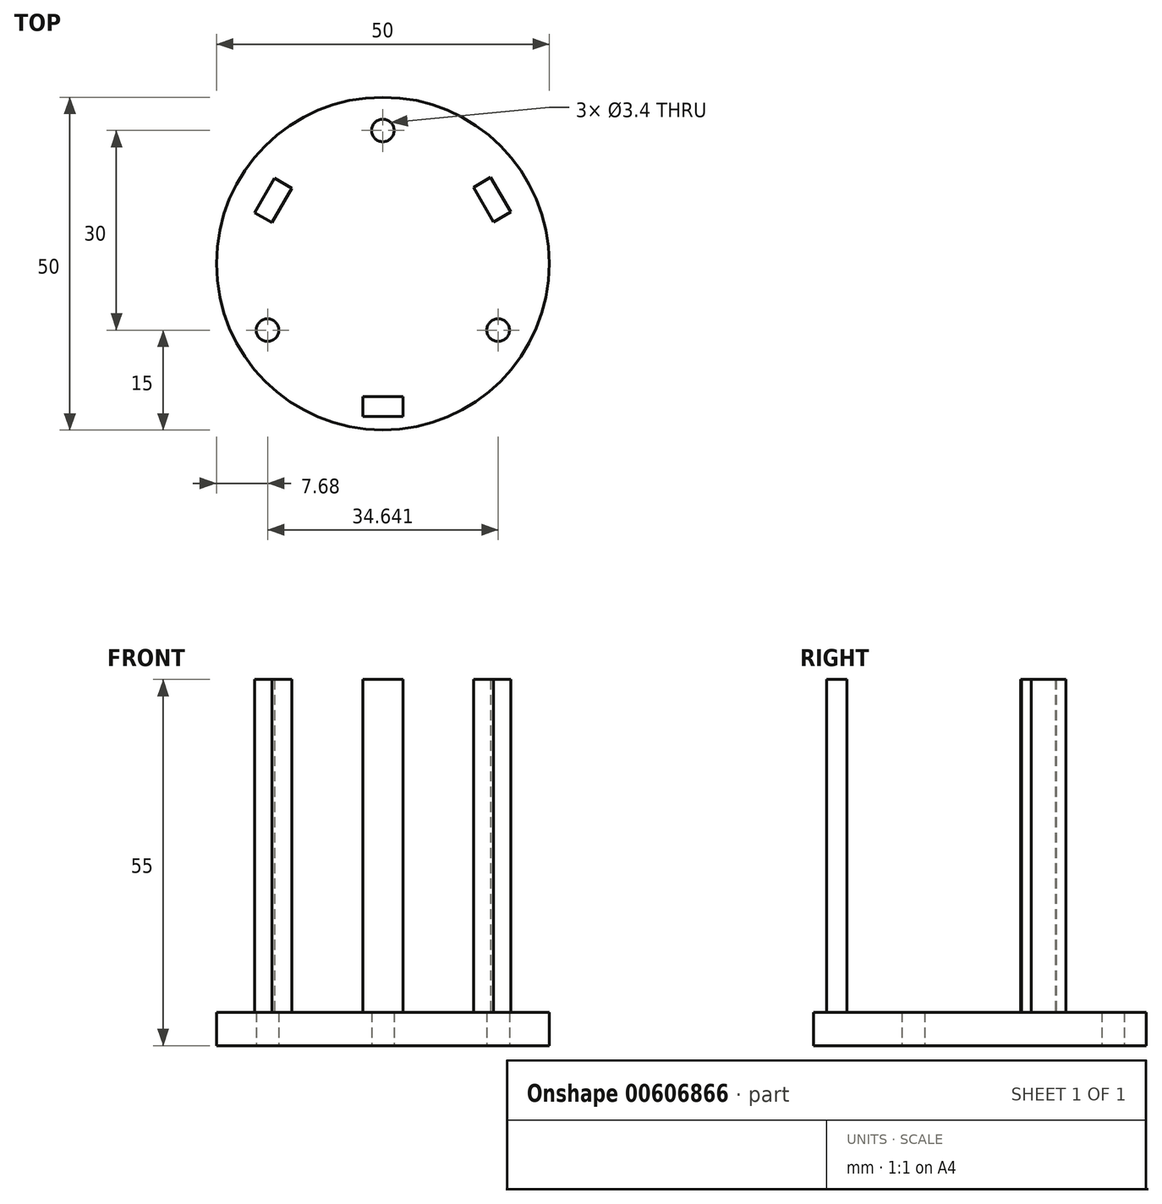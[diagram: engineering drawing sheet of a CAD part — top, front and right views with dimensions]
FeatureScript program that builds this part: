
annotation { "Feature Type Name" : "Feature", "Feature Type Description" : "" }
export const myFeature = defineFeature(function(context is Context, id is Id, definition is map)
    precondition{}
    {
        {
            var Q0;
            Q0=qCreatedBy(makeId("Top.planeOp"),FACE);
            var sketch = newSketch(context, id + "F0", { "sketchPlane" : qUnion([Q0])});
            skCircle(sketch, "E0", {"center": v(0, 0) * mm, "radius": 25 * mm});
            skCircle(sketch, "E1", {"center": v(0, 0) * mm, "radius": 20 * mm, "construction": true});
            skCircle(sketch, "E2", {"center": v(0, 20) * mm, "radius": 1.7 * mm});
            skCircle(sketch, "E3.1.0", {"center": v(-17.32, -10) * mm, "radius": 1.7 * mm});
            skCircle(sketch, "E3.2.0", {"center": v(17.32, -10) * mm, "radius": 1.7 * mm});
            skSolve(sketch);
        }
        {
            var Q0;
            Q0=makeQuery(id+"F0.imprint","IMPRINT",FACE,{"disambiguationData":[TD([[makeQuery(id+"F0.imprint","IMPRINT",EDGE,{"derivedFrom":sQuery(id+"F0.wireOp",EDGE,"E0")}),1.0]])]});
            extrude(context, id + "F1", {"entities" : qUnion([Q0]), "depth" : 5 * mm, "offsetDistance" : 25 * mm});
        }
        {
            var Q0;
            Q0=qCreatedBy(makeId("Top.planeOp"),FACE);
            cPlane(context, id + "F2", {"entities" : qUnion([Q0]), "cplaneType" : CPlaneType.OFFSET, "offset" : 50 * mm, "width" : 150 * mm, "height" : 150 * mm});
        }
        {
            var Q0;
            Q0=makeQuery(id+"F1.opExtrude","CAP_FACE",FACE,{"disambiguationData":[OSD([sQuery(id+"F0.wireOp",EDGE,"E0"),sQuery(id+"F0.wireOp",EDGE,"E2"),sQuery(id+"F0.wireOp",EDGE,"E3.1.0"),sQuery(id+"F0.wireOp",EDGE,"E3.2.0")])],"isStart":false});
            var sketch = newSketch(context, id + "F3", { "sketchPlane" : qUnion([Q0])});
            skCircle(sketch, "E4.cCircle", {"center": v(0, 0) * mm, "radius": 17.5 * mm, "construction": true});
            skLineSegment(sketch, "E4.0", {"start": v(-10.1, 17.5) * mm, "end": v(10.1, 17.5) * mm});
            skLineSegment(sketch, "E4.1", {"start": v(10.1, 17.5) * mm, "end": v(20.2, 0) * mm});
            skLineSegment(sketch, "E4.2", {"start": v(20.2, 0) * mm, "end": v(10.1, -17.5) * mm});
            skLineSegment(sketch, "E4.3", {"start": v(10.1, -17.5) * mm, "end": v(-10.1, -17.5) * mm});
            skLineSegment(sketch, "E4.4", {"start": v(-10.1, -17.5) * mm, "end": v(-20.2, 0) * mm});
            skLineSegment(sketch, "E4.5", {"start": v(-20.2, 0) * mm, "end": v(-10.1, 17.5) * mm});
            skPoint(sketch, "E4.0.midPoint", {"position": v(0, 17.5) * mm});
            skLineSegment(sketch, "E5", {"start": v(13.6, 11.44) * mm, "end": v(16.2, 12.94) * mm});
            skLineSegment(sketch, "E6", {"start": v(16.2, 12.94) * mm, "end": v(19.2, 7.74) * mm});
            skLineSegment(sketch, "E7", {"start": v(19.2, 7.74) * mm, "end": v(16.6, 6.24) * mm});
            skLineSegment(sketch, "E8", {"start": v(-16.66, 6.15) * mm, "end": v(-19.25, 7.65) * mm});
            skLineSegment(sketch, "E9", {"start": v(-19.25, 7.65) * mm, "end": v(-16.25, 12.85) * mm});
            skLineSegment(sketch, "E10", {"start": v(-16.25, 12.85) * mm, "end": v(-13.66, 11.35) * mm});
            skPoint(sketch, "E11", {"position": v(-15.16, 8.75) * mm});
            skLineSegment(sketch, "E12", {"start": v(-16.66, 6.15) * mm, "end": v(-13.66, 11.35) * mm});
            skLineSegment(sketch, "E13", {"start": v(-5.87, -17.5) * mm, "end": v(5.87, -17.5) * mm});
            skLineSegment(sketch, "E14", {"start": v(13.6, 11.44) * mm, "end": v(16.6, 6.24) * mm});
            skPoint(sketch, "E15", {"position": v(0, -17.5) * mm});
            skPoint(sketch, "E16", {"position": v(15.1, 8.84) * mm});
            skPoint(sketch, "E17", {"position": v(15.16, 8.75) * mm});
            skLineSegment(sketch, "E18", {"start": v(-5.87, -17.5) * mm, "end": v(-5.87, -20) * mm, "construction": true});
            skLineSegment(sketch, "E19", {"start": v(-5.87, -20) * mm, "end": v(5.87, -20) * mm, "construction": true});
            skLineSegment(sketch, "E20", {"start": v(5.87, -20) * mm, "end": v(5.87, -17.5) * mm, "construction": true});
            skLineSegment(sketch, "E21", {"start": v(-3, -20) * mm, "end": v(3, -20) * mm});
            skLineSegment(sketch, "E22", {"start": v(3, -20) * mm, "end": v(3, -23) * mm});
            skLineSegment(sketch, "E23", {"start": v(3, -23) * mm, "end": v(-3, -23) * mm});
            skLineSegment(sketch, "E24", {"start": v(-3, -23) * mm, "end": v(-3, -20) * mm});
            skPoint(sketch, "E25", {"position": v(0, -23) * mm});
            skSolve(sketch);
        }
        {
            var Q0;
            Q0=makeQuery(id+"F3.imprint","IMPRINT",FACE,{"disambiguationData":[TD([[makeQuery(id+"F3.imprint","IMPRINT",EDGE,{"derivedFrom":sQuery(id+"F3.wireOp",EDGE,"E8")}),-1.0]])]});
            var Q1;
            Q1=makeQuery(id+"F3.imprint","IMPRINT",FACE,{"disambiguationData":[TD([[makeQuery(id+"F3.imprint","IMPRINT",EDGE,{"derivedFrom":sQuery(id+"F3.wireOp",EDGE,"E5")}),-1.0]])]});
            var Q2;
            Q2=makeQuery(id+"F3.imprint","IMPRINT",FACE,{"disambiguationData":[TD([[makeQuery(id+"F3.imprint","IMPRINT",EDGE,{"derivedFrom":sQuery(id+"F3.wireOp",EDGE,"EmWx3WfU-mLyR-nX2W-iOl9-O7EFhruVmHkr")}),1.0]])]});
            var Q3;
            Q3=makeQuery(id+"F3.imprint","IMPRINT",FACE,{"disambiguationData":[TD([[makeQuery(id+"F3.imprint","IMPRINT",EDGE,{"derivedFrom":sQuery(id+"F3.wireOp",EDGE,"E21")}),-1.0]])]});
            extrude(context, id + "F4", {"entities" : qUnion([Q0, Q1, Q2, Q3]), "operationType" : NewBodyOperationType.ADD, "depth" : 50 * mm, "offsetDistance" : 25 * mm});
        }
    });
